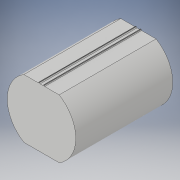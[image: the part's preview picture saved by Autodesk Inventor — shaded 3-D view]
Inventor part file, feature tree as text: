
AUTODESK INVENTOR PART (.ipt)
format: ipt  version: 2017 (Build 210142000, 142)  size: 129,024 bytes
history: native  units: in
note: dims shown in document units (in); Inventor stores cm internally (conversion verified against a paired STEP export)
features: other x1, sketch x1
ambient origin geometry x8: Origin, YZ Plane, XZ Plane, XY Plane, X Axis, Y Axis, Z Axis, Center Point
bodies: Solid1 (feature_tree)
feature tree (2):
  other  "corridor"
  sketch  "Sketch1"  dims[d0=6.6667in d1=4.0in d2=1.0in d3=11.0in d4=0.0in d7=1.0in d23=0.5833in d26=0.125in d27=3.8873in d28=3.8873in d30=1.7083in d39=0.0625in d40=0.0625in d41=1.6458in d51=0.25in d52=0.125in d53=0.0892in d54=0.0884in d55=45.0deg d56=3.3333in]
